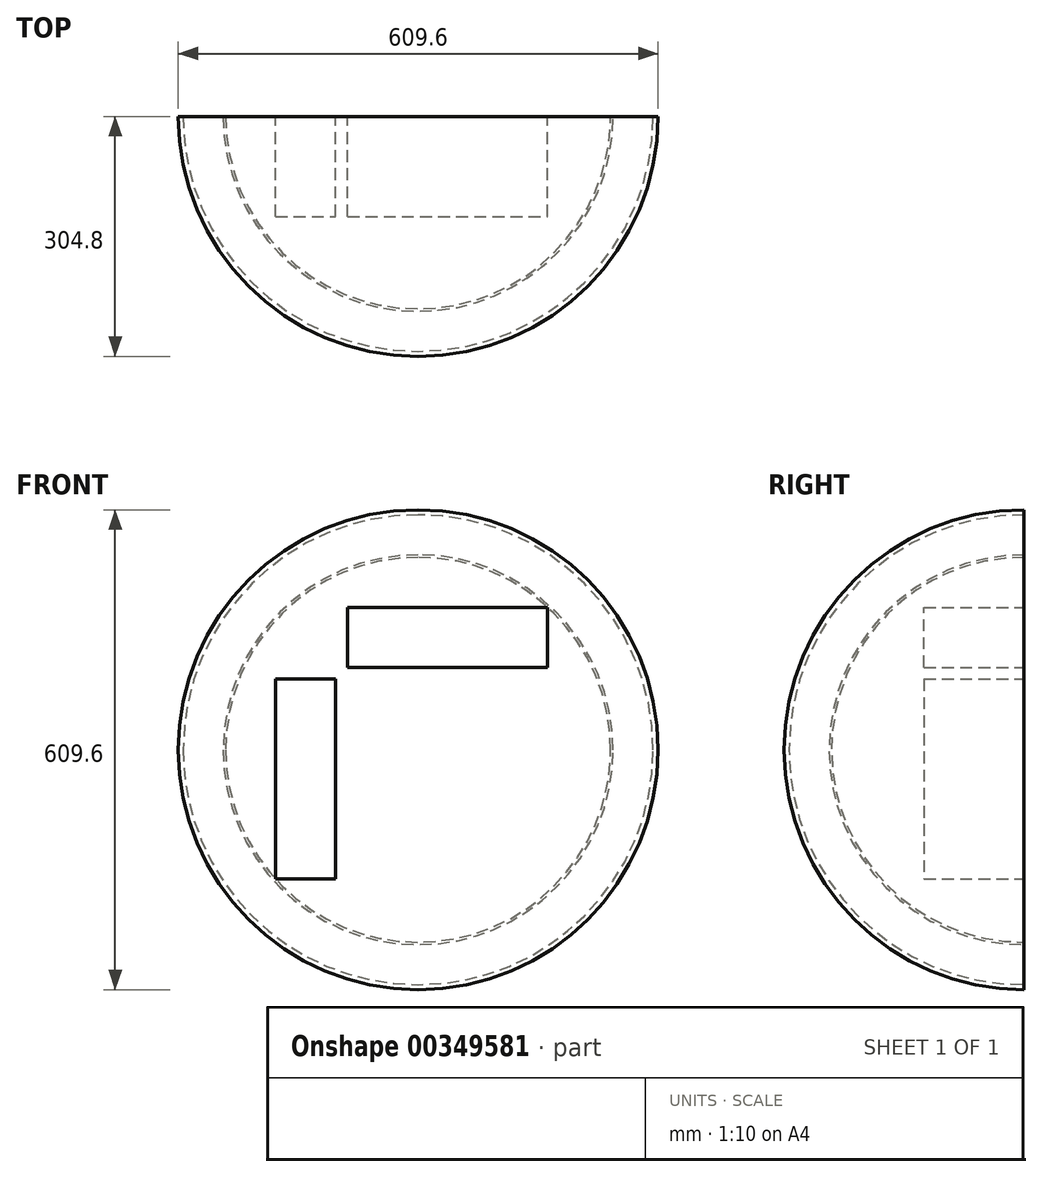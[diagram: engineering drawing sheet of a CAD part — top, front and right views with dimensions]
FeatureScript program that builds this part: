
annotation { "Feature Type Name" : "Feature", "Feature Type Description" : "" }
export const myFeature = defineFeature(function(context is Context, id is Id, definition is map)
    precondition{}
    {
        {
            var Q0;
            Q0=qCreatedBy(makeId("Front.planeOp"),FACE);
            var sketch = newSketch(context, id + "F0", { "sketchPlane" : qUnion([Q0])});
            skArc(sketch, "E0", {"start": v(304.8, 0) * mm, "mid": v(0, 304.8) * mm, "end": v(-304.8, 0) * mm});
            skLineSegment(sketch, "E1", {"start": v(-304.8, 0) * mm, "end": v(304.8, 0) * mm});
            skArc(sketch, "E2.0", {"start": v(298.45, 0) * mm, "mid": v(0, 298.45) * mm, "end": v(-298.45, 0) * mm});
            skSolve(sketch);
        }
        {
            var Q0;
            Q0=makeQuery(id+"F0.imprint","IMPRINT",FACE,{"disambiguationData":[TD([[makeQuery(id+"F0.imprint","IMPRINT",EDGE,{"derivedFrom":sQuery(id+"F0.wireOp",EDGE,"E0")}),1.0]])]});
            var Q1;
            Q1=sQuery(id+"F0.wireOp",EDGE,"E1");
            revolve(context, id + "F1", {"entities" : qUnion([Q0]), "axis" : qUnion([Q1]), "revolveType" : RevolveType.ONE_DIRECTION, "angle" : 180 * degree});
        }
        {
            var Q0;
            Q0=qCreatedBy(makeId("Front.planeOp"),FACE);
            var sketch = newSketch(context, id + "F2", { "sketchPlane" : qUnion([Q0])});
            skArc(sketch, "E3", {"start": v(247.65, 0) * mm, "mid": v(0, 247.65) * mm, "end": v(-247.65, 0) * mm});
            skLineSegment(sketch, "E4", {"start": v(247.65, 0) * mm, "end": v(-247.65, 0) * mm});
            skArc(sketch, "E5.0", {"start": v(244.47, 0) * mm, "mid": v(0, 244.47) * mm, "end": v(-244.47, 0) * mm});
            skSolve(sketch);
        }
        {
            var Q0;
            {var subQ0=sQuery(id+"F2.wireOp",EDGE,"E3");Q0=makeQuery(id+"F2.imprint","IMPRINT",FACE,{"disambiguationData":[TD([[makeQuery(id+"F2.imprint","IMPRINT",EDGE,{"derivedFrom":subQ0}),1.0]])]});}
            var Q1;
            Q1=sQuery(id+"F2.wireOp",EDGE,"E4");
            revolve(context, id + "F3", {"entities" : qUnion([Q0]), "axis" : qUnion([Q1]), "revolveType" : RevolveType.ONE_DIRECTION, "oppositeDirection" : true, "angle" : 180 * degree});
        }
        {
            var Q0;
            Q0=qCreatedBy(makeId("Front.planeOp"),FACE);
            var sketch = newSketch(context, id + "F4", { "sketchPlane" : qUnion([Q0])});
            skLineSegment(sketch, "E6.bottom", {"start": v(-180.97, 89.63) * mm, "end": v(-104.77, 89.63) * mm});
            skLineSegment(sketch, "E6.top", {"start": v(-180.97, -164.37) * mm, "end": v(-104.77, -164.37) * mm});
            skLineSegment(sketch, "E6.left", {"start": v(-180.97, 89.63) * mm, "end": v(-180.97, -164.37) * mm});
            skLineSegment(sketch, "E6.right", {"start": v(-104.77, 89.63) * mm, "end": v(-104.77, -164.37) * mm});
            skLineSegment(sketch, "E7.bottom", {"start": v(-89.63, 104.78) * mm, "end": v(-89.63, 180.97) * mm});
            skLineSegment(sketch, "E7.top", {"start": v(164.37, 104.78) * mm, "end": v(164.37, 180.97) * mm});
            skLineSegment(sketch, "E7.left", {"start": v(-89.63, 104.78) * mm, "end": v(164.37, 104.78) * mm});
            skLineSegment(sketch, "E7.right", {"start": v(-89.63, 180.97) * mm, "end": v(164.37, 180.97) * mm});
            skSolve(sketch);
        }
        {
            var Q0;
            Q0 = qSketchRegion(id + "F4", true);
            extrude(context, id + "F5", {"entities" : qUnion([Q0]), "depth" : 127 * mm});
        }
    });
